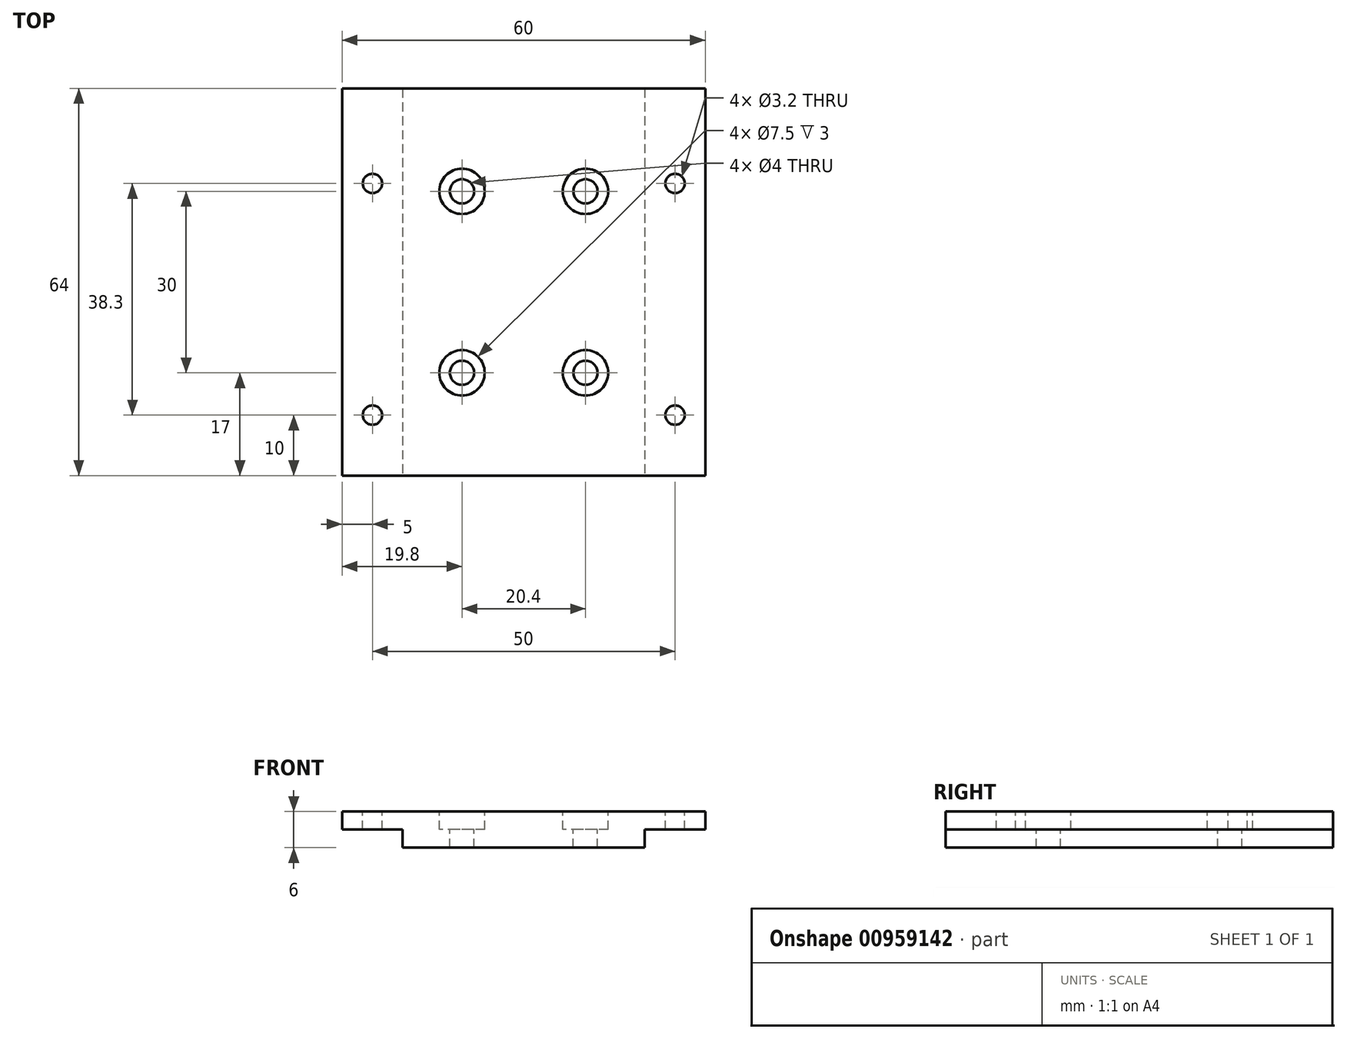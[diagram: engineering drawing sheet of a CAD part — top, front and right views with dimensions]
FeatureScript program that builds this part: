
annotation { "Feature Type Name" : "Feature", "Feature Type Description" : "" }
export const myFeature = defineFeature(function(context is Context, id is Id, definition is map)
    precondition{}
    {
        {
            var Q0;
            Q0=qCreatedBy(makeId("Top.planeOp"),FACE);
            var sketch = newSketch(context, id + "F0", { "sketchPlane" : qUnion([Q0])});
            skLineSegment(sketch, "E0.bottom", {"start": v(-20, 32) * mm, "end": v(20, 32) * mm});
            skLineSegment(sketch, "E0.top", {"start": v(-20, -32) * mm, "end": v(20, -32) * mm});
            skLineSegment(sketch, "E0.left", {"start": v(-20, 32) * mm, "end": v(-20, -32) * mm});
            skLineSegment(sketch, "E0.right", {"start": v(20, 32) * mm, "end": v(20, -32) * mm});
            skSolve(sketch);
        }
        {
            var Q0;
            Q0=makeQuery(id+"F0.imprint","IMPRINT",FACE,{"disambiguationData":[TD([[makeQuery(id+"F0.imprint","IMPRINT",EDGE,{"derivedFrom":sQuery(id+"F0.wireOp",EDGE,"E0.bottom")}),-1.0]])]});
            extrude(context, id + "F1", {"entities" : qUnion([Q0]), "depth" : 3 * mm, "offsetDistance" : 25 * mm});
        }
        {
            var Q0;
            Q0=makeQuery(id+"F1.opExtrude","CAP_FACE",FACE,{"disambiguationData":[OSD([sQuery(id+"F0.wireOp",EDGE,"E0.bottom"),sQuery(id+"F0.wireOp",EDGE,"E0.top"),sQuery(id+"F0.wireOp",EDGE,"E0.left"),sQuery(id+"F0.wireOp",EDGE,"E0.right")])],"isStart":false});
            var sketch = newSketch(context, id + "F2", { "sketchPlane" : qUnion([Q0])});
            skLineSegment(sketch, "E1.bottom", {"start": v(30, 32) * mm, "end": v(-30, 32) * mm});
            skLineSegment(sketch, "E1.top", {"start": v(30, -32) * mm, "end": v(-30, -32) * mm});
            skLineSegment(sketch, "E1.left", {"start": v(30, 32) * mm, "end": v(30, -32) * mm});
            skLineSegment(sketch, "E1.right", {"start": v(-30, 32) * mm, "end": v(-30, -32) * mm});
            skSolve(sketch);
        }
        {
            var Q0;
            {var subQ2=sQuery(id+"F2.wireOp",EDGE,"E1.right");Q0=makeQuery(id+"F2.imprint","IMPRINT",FACE,{"disambiguationData":[TD([[makeQuery(id+"F2.imprint","IMPRINT",EDGE,{"derivedFrom":subQ2}),1.0]])]});}
            var Q1;
            {var subQ1=makeQuery(id+"F1.opExtrude","CAP_EDGE",EDGE,{"disambiguationData":[OSD([sQuery(id+"F0.wireOp",EDGE,"E0.left")])],"isStart":false});Q1=makeQuery(id+"F2.imprint","IMPRINT",FACE,{"disambiguationData":[TD([[makeQuery(id+"F2.imprint","IMPRINT",EDGE,{"derivedFrom":subQ1}),1.0]])]});}
            var Q2;
            {var subQ2=sQuery(id+"F2.wireOp",EDGE,"E1.left");Q2=makeQuery(id+"F2.imprint","IMPRINT",FACE,{"disambiguationData":[TD([[makeQuery(id+"F2.imprint","IMPRINT",EDGE,{"derivedFrom":subQ2}),-1.0]])]});}
            extrude(context, id + "F3", {"entities" : qUnion([Q0, Q1, Q2]), "operationType" : NewBodyOperationType.ADD, "depth" : 3 * mm, "offsetDistance" : 25 * mm});
        }
        {
            var Q0;
            Q0=makeQuery(id+"F3.opExtrude","CAP_FACE",FACE,{"disambiguationData":[OSD([sQuery(id+"F2.wireOp",EDGE,"E1.bottom"),sQuery(id+"F2.wireOp",EDGE,"E1.top"),sQuery(id+"F2.wireOp",EDGE,"E1.left"),sQuery(id+"F2.wireOp",EDGE,"E1.right")])],"isStart":false});
            var sketch = newSketch(context, id + "F4", { "sketchPlane" : qUnion([Q0])});
            skCircle(sketch, "E2", {"center": v(-25, 16.3) * mm, "radius": 1.6 * mm});
            skSolve(sketch);
        }
        {
            var Q0;
            Q0=makeQuery(id+"F4.imprint","IMPRINT",FACE,{"disambiguationData":[TD([[makeQuery(id+"F4.imprint","IMPRINT",EDGE,{"derivedFrom":sQuery(id+"F4.wireOp",EDGE,"E2")}),1.0]])]});
            extrude(context, id + "F5", {"entities" : qUnion([Q0]), "operationType" : NewBodyOperationType.REMOVE, "oppositeDirection" : true, "depth" : 25 * mm, "offsetDistance" : 25 * mm});
        }
        {
            var Q0;
            Q0=makeQuery(id+"F3.opExtrude","CAP_FACE",FACE,{"disambiguationData":[OSD([sQuery(id+"F2.wireOp",EDGE,"E1.bottom"),sQuery(id+"F2.wireOp",EDGE,"E1.top"),sQuery(id+"F2.wireOp",EDGE,"E1.left"),sQuery(id+"F2.wireOp",EDGE,"E1.right")])],"isStart":false});
            var sketch = newSketch(context, id + "F6", { "sketchPlane" : qUnion([Q0])});
            skCircle(sketch, "E3", {"center": v(-25, -22) * mm, "radius": 1.6 * mm});
            skCircle(sketch, "E4", {"center": v(25, 16.3) * mm, "radius": 1.6 * mm});
            skCircle(sketch, "E5", {"center": v(25, -22) * mm, "radius": 1.6 * mm});
            skSolve(sketch);
        }
        {
            var Q0;
            Q0=makeQuery(id+"F6.imprint","IMPRINT",FACE,{"disambiguationData":[TD([[makeQuery(id+"F6.imprint","IMPRINT",EDGE,{"derivedFrom":sQuery(id+"F6.wireOp",EDGE,"E3")}),1.0]])]});
            var Q1;
            Q1=makeQuery(id+"F6.imprint","IMPRINT",FACE,{"disambiguationData":[TD([[makeQuery(id+"F6.imprint","IMPRINT",EDGE,{"derivedFrom":sQuery(id+"F6.wireOp",EDGE,"E5")}),1.0]])]});
            var Q2;
            Q2=makeQuery(id+"F6.imprint","IMPRINT",FACE,{"disambiguationData":[TD([[makeQuery(id+"F6.imprint","IMPRINT",EDGE,{"derivedFrom":sQuery(id+"F6.wireOp",EDGE,"E4")}),1.0]])]});
            extrude(context, id + "F7", {"entities" : qUnion([Q0, Q1, Q2]), "operationType" : NewBodyOperationType.REMOVE, "oppositeDirection" : true, "depth" : 25 * mm, "offsetDistance" : 25 * mm});
        }
        {
            var Q0;
            Q0=makeQuery(id+"F3.opExtrude","CAP_FACE",FACE,{"disambiguationData":[OSD([sQuery(id+"F2.wireOp",EDGE,"E1.bottom"),sQuery(id+"F2.wireOp",EDGE,"E1.top"),sQuery(id+"F2.wireOp",EDGE,"E1.left"),sQuery(id+"F2.wireOp",EDGE,"E1.right")])],"isStart":false});
            var sketch = newSketch(context, id + "F8", { "sketchPlane" : qUnion([Q0])});
            skCircle(sketch, "E6", {"center": v(-10.2, 15) * mm, "radius": 3.75 * mm});
            skCircle(sketch, "E7", {"center": v(10.2, 15) * mm, "radius": 3.75 * mm});
            skCircle(sketch, "E8", {"center": v(-10.2, -15) * mm, "radius": 3.75 * mm});
            skCircle(sketch, "E9", {"center": v(10.2, -15) * mm, "radius": 3.75 * mm});
            skSolve(sketch);
        }
        {
            var Q0;
            Q0=makeQuery(id+"F8.imprint","IMPRINT",FACE,{"disambiguationData":[TD([[makeQuery(id+"F8.imprint","IMPRINT",EDGE,{"derivedFrom":sQuery(id+"F8.wireOp",EDGE,"E8")}),1.0]])]});
            var Q1;
            Q1=makeQuery(id+"F8.imprint","IMPRINT",FACE,{"disambiguationData":[TD([[makeQuery(id+"F8.imprint","IMPRINT",EDGE,{"derivedFrom":sQuery(id+"F8.wireOp",EDGE,"E9")}),1.0]])]});
            var Q2;
            Q2=makeQuery(id+"F8.imprint","IMPRINT",FACE,{"disambiguationData":[TD([[makeQuery(id+"F8.imprint","IMPRINT",EDGE,{"derivedFrom":sQuery(id+"F8.wireOp",EDGE,"E7")}),1.0]])]});
            var Q3;
            Q3=makeQuery(id+"F8.imprint","IMPRINT",FACE,{"disambiguationData":[TD([[makeQuery(id+"F8.imprint","IMPRINT",EDGE,{"derivedFrom":sQuery(id+"F8.wireOp",EDGE,"E6")}),1.0]])]});
            extrude(context, id + "F9", {"entities" : qUnion([Q0, Q1, Q2, Q3]), "operationType" : NewBodyOperationType.REMOVE, "oppositeDirection" : true, "depth" : 3 * mm, "offsetDistance" : 25 * mm});
        }
        {
            var Q0;
            Q0=makeQuery(id+"F9.boolean.opBoolean","COPY",FACE,{"derivedFrom":makeQuery(id+"F9.opExtrude","CAP_FACE",FACE,{"disambiguationData":[OSD([sQuery(id+"F8.wireOp",EDGE,"E8")])],"isStart":false})});
            var sketch = newSketch(context, id + "F10", { "sketchPlane" : qUnion([Q0])});
            skCircle(sketch, "E10", {"center": v(-10.2, -15) * mm, "radius": 2 * mm});
            skCircle(sketch, "E11", {"center": v(10.2, -15) * mm, "radius": 2 * mm});
            skCircle(sketch, "E12", {"center": v(10.2, 15) * mm, "radius": 2 * mm});
            skCircle(sketch, "E13", {"center": v(-10.2, 15) * mm, "radius": 2 * mm});
            skSolve(sketch);
        }
        {
            var Q0;
            Q0=makeQuery(id+"F10.imprint","IMPRINT",FACE,{"disambiguationData":[TD([[makeQuery(id+"F10.imprint","IMPRINT",EDGE,{"derivedFrom":sQuery(id+"F10.wireOp",EDGE,"E10")}),1.0]])]});
            var Q1;
            Q1=makeQuery(id+"F10.imprint","IMPRINT",FACE,{"disambiguationData":[TD([[makeQuery(id+"F10.imprint","IMPRINT",EDGE,{"derivedFrom":sQuery(id+"F10.wireOp",EDGE,"E13")}),1.0]])]});
            var Q2;
            Q2=makeQuery(id+"F10.imprint","IMPRINT",FACE,{"disambiguationData":[TD([[makeQuery(id+"F10.imprint","IMPRINT",EDGE,{"derivedFrom":sQuery(id+"F10.wireOp",EDGE,"E12")}),1.0]])]});
            var Q3;
            Q3=makeQuery(id+"F10.imprint","IMPRINT",FACE,{"disambiguationData":[TD([[makeQuery(id+"F10.imprint","IMPRINT",EDGE,{"derivedFrom":sQuery(id+"F10.wireOp",EDGE,"E11")}),1.0]])]});
            extrude(context, id + "F11", {"entities" : qUnion([Q0, Q1, Q2, Q3]), "operationType" : NewBodyOperationType.REMOVE, "oppositeDirection" : true, "depth" : 25 * mm, "offsetDistance" : 25 * mm});
        }
    });
